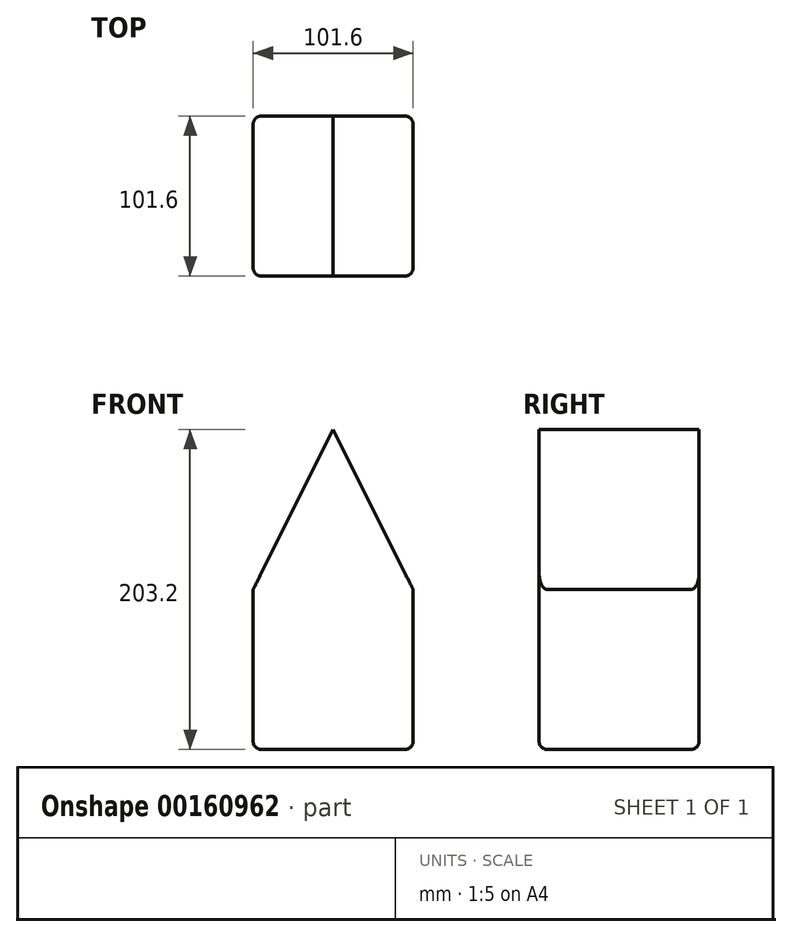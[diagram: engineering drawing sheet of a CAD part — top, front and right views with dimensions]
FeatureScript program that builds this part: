
annotation { "Feature Type Name" : "Feature", "Feature Type Description" : "" }
export const myFeature = defineFeature(function(context is Context, id is Id, definition is map)
    precondition{}
    {
        {
            var Q0;
            Q0=qCreatedBy(makeId("Top.planeOp"),FACE);
            var sketch = newSketch(context, id + "F0", { "sketchPlane" : qUnion([Q0])});
            skLineSegment(sketch, "E0.bottom", {"start": v(50.8, -50.8) * mm, "end": v(-50.8, -50.8) * mm});
            skLineSegment(sketch, "E0.top", {"start": v(50.8, 50.8) * mm, "end": v(-50.8, 50.8) * mm});
            skLineSegment(sketch, "E0.left", {"start": v(50.8, -50.8) * mm, "end": v(50.8, 50.8) * mm});
            skLineSegment(sketch, "E0.right", {"start": v(-50.8, -50.8) * mm, "end": v(-50.8, 50.8) * mm});
            skPoint(sketch, "E0.middle", {"position": v(0, 0) * mm});
            skSolve(sketch);
        }
        {
            var Q0;
            Q0 = qSketchRegion(id + "F0", true);
            extrude(context, id + "F1", {"entities" : qUnion([Q0]), "depth" : 101.6 * mm});
        }
        {
            var Q0;
            Q0=makeQuery(id+"F1.opExtrude","CAP_FACE",FACE,{"disambiguationData":[OSD([sQuery(id+"F0.wireOp",EDGE,"E0.bottom"),sQuery(id+"F0.wireOp",EDGE,"E0.top"),sQuery(id+"F0.wireOp",EDGE,"E0.left"),sQuery(id+"F0.wireOp",EDGE,"E0.right")])],"isStart":false});
            var sketch = newSketch(context, id + "F2", { "sketchPlane" : qUnion([Q0])});
            skLineSegment(sketch, "E1.bottom", {"start": v(-50.8, 50.8) * mm, "end": v(50.8, 50.8) * mm});
            skLineSegment(sketch, "E1.top", {"start": v(-50.8, -50.8) * mm, "end": v(50.8, -50.8) * mm});
            skLineSegment(sketch, "E1.left", {"start": v(-50.8, 50.8) * mm, "end": v(-50.8, -50.8) * mm});
            skLineSegment(sketch, "E1.right", {"start": v(50.8, 50.8) * mm, "end": v(50.8, -50.8) * mm});
            skSolve(sketch);
        }
        {
            var Q0;
            Q0 = qSketchRegion(id + "F2", true);
            extrude(context, id + "F3", {"entities" : qUnion([Q0]), "operationType" : NewBodyOperationType.ADD, "depth" : 101.6 * mm});
        }
        {
            var Q0;
            Q0=makeQuery(id+"F3.boolean.opBoolean","MERGE",FACE,{"derivedFrom":[makeQuery(id+"F1.opExtrude","SWEPT_FACE",FACE,{"disambiguationData":[OSD([sQuery(id+"F0.wireOp",EDGE,"E0.top")])]}),makeQuery(id+"F3.opExtrude","SWEPT_FACE",FACE,{"disambiguationData":[OSD([sQuery(id+"F2.wireOp",EDGE,"E1.bottom")])]})]});
            var sketch = newSketch(context, id + "F4", { "sketchPlane" : qUnion([Q0])});
            skLineSegment(sketch, "E2", {"start": v(0, 203.2) * mm, "end": v(50.8, 101.6) * mm});
            skLineSegment(sketch, "E3", {"start": v(0, 203.2) * mm, "end": v(-50.8, 101.6) * mm});
            skLineSegment(sketch, "E4", {"start": v(-50.8, 101.6) * mm, "end": v(-50.8, 203.2) * mm});
            skLineSegment(sketch, "E5", {"start": v(-50.8, 203.2) * mm, "end": v(0, 203.2) * mm});
            skLineSegment(sketch, "E6", {"start": v(50.8, 203.2) * mm, "end": v(50.8, 101.6) * mm});
            skSolve(sketch);
        }
        {
            var Q0;
            Q0=makeQuery(id+"F4.imprint","IMPRINT",FACE,{"disambiguationData":[TD([[makeQuery(id+"F4.imprint","IMPRINT",EDGE,{"derivedFrom":sQuery(id+"F4.wireOp",EDGE,"E3")}),-1.0]])]});
            var Q1;
            {var subQ0=sQuery(id+"F4.wireOp",EDGE,"E2");Q1=makeQuery(id+"F4.imprint","IMPRINT",FACE,{"disambiguationData":[TD([[makeQuery(id+"F4.imprint","IMPRINT",EDGE,{"derivedFrom":subQ0}),1.0]])]});}
            extrude(context, id + "F5", {"entities" : qUnion([Q0, Q1]), "operationType" : NewBodyOperationType.REMOVE, "oppositeDirection" : true, "depth" : 101.6 * mm});
        }
        {
            var Q0;
            Q0=makeQuery(id+"F5.boolean.opBoolean","COPY",EDGE,{"derivedFrom":makeQuery(id+"F5.opExtrude","CAP_EDGE",EDGE,{"disambiguationData":[OSD([sQuery(id+"F4.wireOp",EDGE,"E3")])],"isStart":true})});
            var Q1;
            Q1=makeQuery(id+"F5.boolean.opBoolean","COPY",EDGE,{"derivedFrom":makeQuery(id+"F5.opExtrude","SWEPT_EDGE",EDGE,{"disambiguationData":[OSD([sQuery(id+"F0.wireOp",EDGE,"E0.top"),sQuery(id+"F0.wireOp",EDGE,"E0.left"),sQuery(id+"F2.wireOp",EDGE,"E1.bottom"),sQuery(id+"F2.wireOp",EDGE,"E1.right"),sQuery(id+"F4.wireOp",EDGE,"E3"),sQuery(id+"F4.wireOp",EDGE,"E4")])]})});
            var Q2;
            Q2=makeQuery(id+"F3.boolean.opBoolean","MERGE",EDGE,{"derivedFrom":[makeQuery(id+"F1.opExtrude","SWEPT_EDGE",EDGE,{"disambiguationData":[OSD([sQuery(id+"F0.wireOp",EDGE,"E0.top"),sQuery(id+"F0.wireOp",EDGE,"E0.left")])]}),makeQuery(id+"F3.opExtrude","SWEPT_EDGE",EDGE,{"disambiguationData":[OSD([sQuery(id+"F2.wireOp",EDGE,"E1.bottom"),sQuery(id+"F2.wireOp",EDGE,"E1.right")])]})]});
            var Q3;
            Q3=makeQuery(id+"F5.boolean.opBoolean","COPY",EDGE,{"derivedFrom":makeQuery(id+"F5.opExtrude","SWEPT_EDGE",EDGE,{"disambiguationData":[OSD([sQuery(id+"F0.wireOp",EDGE,"E0.top"),sQuery(id+"F0.wireOp",EDGE,"E0.right"),sQuery(id+"F2.wireOp",EDGE,"E1.bottom"),sQuery(id+"F2.wireOp",EDGE,"E1.left"),sQuery(id+"F4.wireOp",EDGE,"E2"),sQuery(id+"F4.wireOp",EDGE,"E6")])]})});
            var Q4;
            Q4=makeQuery(id+"F3.boolean.opBoolean","MERGE",EDGE,{"derivedFrom":[makeQuery(id+"F1.opExtrude","SWEPT_EDGE",EDGE,{"disambiguationData":[OSD([sQuery(id+"F0.wireOp",EDGE,"E0.top"),sQuery(id+"F0.wireOp",EDGE,"E0.right")])]}),makeQuery(id+"F3.opExtrude","SWEPT_EDGE",EDGE,{"disambiguationData":[OSD([sQuery(id+"F2.wireOp",EDGE,"E1.bottom"),sQuery(id+"F2.wireOp",EDGE,"E1.left")])]})]});
            var Q5;
            Q5=makeQuery(id+"F1.opExtrude","CAP_EDGE",EDGE,{"disambiguationData":[OSD([sQuery(id+"F0.wireOp",EDGE,"E0.right")])],"isStart":true});
            var Q6;
            {var subQ0=sQuery(id+"F4.wireOp",EDGE,"E5");var subQ1=sQuery(id+"F4.wireOp",EDGE,"E3");var subQ2=sQuery(id+"F4.wireOp",EDGE,"E2");var subQ3=sQuery(id+"F2.wireOp",EDGE,"E1.bottom");Q6=makeQuery(id+"F5.boolean.opBoolean","TWEAK_EDGE",EDGE,{"derivedFrom":[makeQuery(id+"F5.opExtrude","SWEPT_EDGE",EDGE,{"disambiguationData":[OSD([subQ3,subQ2,subQ1,subQ0]),ownerDisambiguation([makeQuery(id+"F5.opExtrude","SWEPT_BODY",BODY,{"disambiguationData":[OSD([subQ3,subQ2,sQuery(id+"F4.wireOp",EDGE,"E6")])]})])]}),makeQuery(id+"F5.opExtrude","SWEPT_EDGE",EDGE,{"disambiguationData":[OSD([subQ3,subQ2,subQ1,subQ0]),ownerDisambiguation([makeQuery(id+"F5.opExtrude","SWEPT_BODY",BODY,{"disambiguationData":[OSD([subQ1,sQuery(id+"F4.wireOp",EDGE,"E4"),subQ0])]})])]})]});}
            var Q7;
            Q7=makeQuery(id+"F1.opExtrude","CAP_EDGE",EDGE,{"disambiguationData":[OSD([sQuery(id+"F0.wireOp",EDGE,"E0.top")])],"isStart":true});
            var Q8;
            Q8=makeQuery(id+"F3.boolean.opBoolean","MERGE",EDGE,{"derivedFrom":[makeQuery(id+"F1.opExtrude","SWEPT_EDGE",EDGE,{"disambiguationData":[OSD([sQuery(id+"F0.wireOp",EDGE,"E0.bottom"),sQuery(id+"F0.wireOp",EDGE,"E0.right")])]}),makeQuery(id+"F3.opExtrude","SWEPT_EDGE",EDGE,{"disambiguationData":[OSD([sQuery(id+"F2.wireOp",EDGE,"E1.top"),sQuery(id+"F2.wireOp",EDGE,"E1.left")])]})]});
            var Q9;
            Q9=makeQuery(id+"F3.boolean.opBoolean","MERGE",EDGE,{"derivedFrom":[makeQuery(id+"F1.opExtrude","SWEPT_EDGE",EDGE,{"disambiguationData":[OSD([sQuery(id+"F0.wireOp",EDGE,"E0.bottom"),sQuery(id+"F0.wireOp",EDGE,"E0.left")])]}),makeQuery(id+"F3.opExtrude","SWEPT_EDGE",EDGE,{"disambiguationData":[OSD([sQuery(id+"F2.wireOp",EDGE,"E1.top"),sQuery(id+"F2.wireOp",EDGE,"E1.right")])]})]});
            var Q10;
            Q10=makeQuery(id+"F5.boolean.opBoolean","COPY",EDGE,{"derivedFrom":makeQuery(id+"F5.opExtrude","CAP_EDGE",EDGE,{"disambiguationData":[OSD([sQuery(id+"F4.wireOp",EDGE,"E2")])],"isStart":false})});
            var Q11;
            Q11=makeQuery(id+"F5.boolean.opBoolean","COPY",EDGE,{"derivedFrom":makeQuery(id+"F5.opExtrude","CAP_EDGE",EDGE,{"disambiguationData":[OSD([sQuery(id+"F4.wireOp",EDGE,"E2")])],"isStart":true})});
            var Q12;
            Q12=makeQuery(id+"F1.opExtrude","CAP_EDGE",EDGE,{"disambiguationData":[OSD([sQuery(id+"F0.wireOp",EDGE,"E0.bottom")])],"isStart":true});
            var Q13;
            Q13=makeQuery(id+"F1.opExtrude","CAP_EDGE",EDGE,{"disambiguationData":[OSD([sQuery(id+"F0.wireOp",EDGE,"E0.left")])],"isStart":true});
            var Q14;
            Q14=makeQuery(id+"F5.boolean.opBoolean","COPY",EDGE,{"derivedFrom":makeQuery(id+"F5.opExtrude","CAP_EDGE",EDGE,{"disambiguationData":[OSD([sQuery(id+"F4.wireOp",EDGE,"E3")])],"isStart":false})});
            fillet(context, id + "F6", {"entities" : qUnion([Q0, Q1, Q2, Q3, Q4, Q5, Q6, Q7, Q8, Q9, Q10, Q11, Q12, Q13, Q14]), "radius" : 5.08 * mm, "tangentPropagation" : true, "allowEdgeOverflow" : false});
        }
    });
